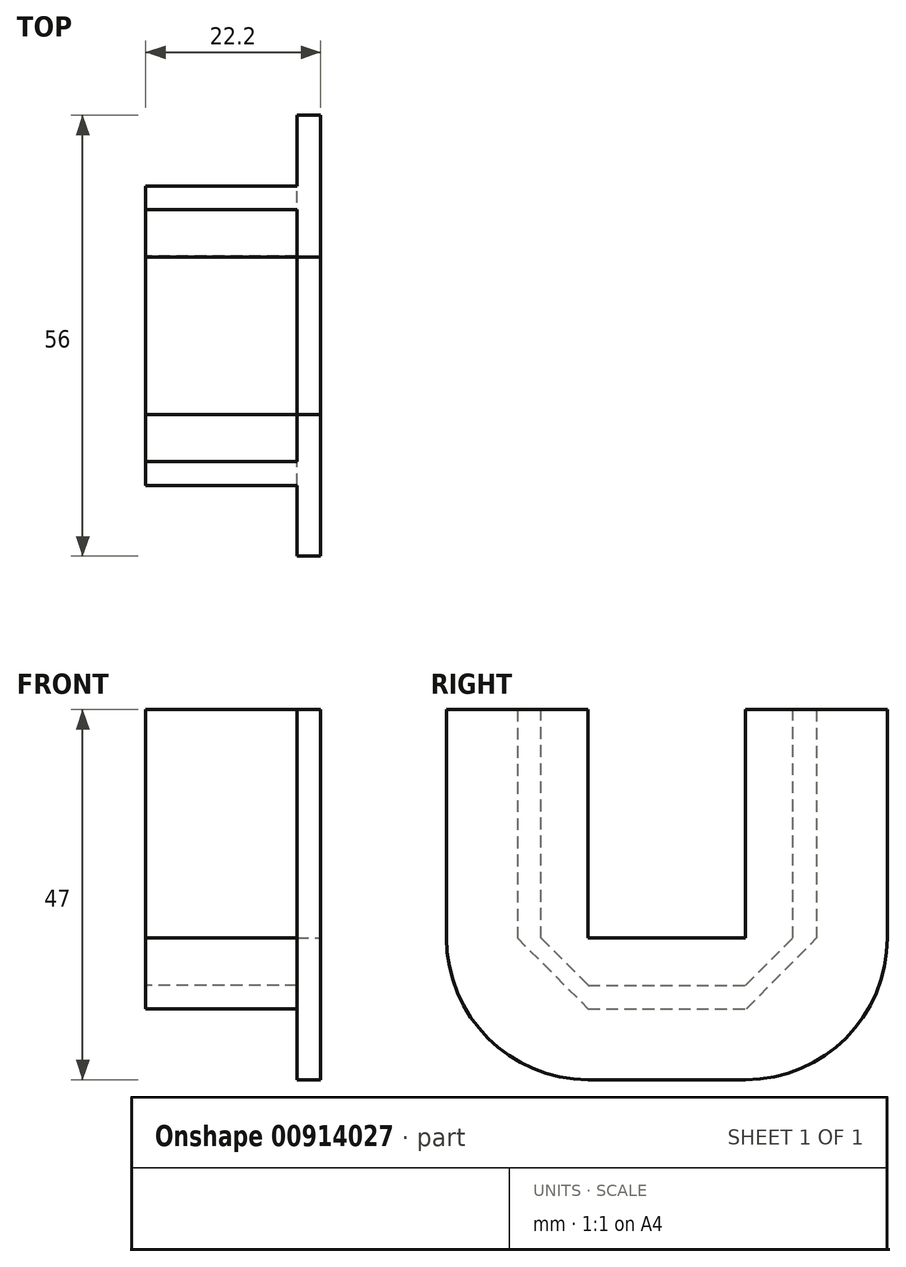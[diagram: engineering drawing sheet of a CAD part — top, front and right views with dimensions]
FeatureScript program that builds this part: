
annotation { "Feature Type Name" : "Feature", "Feature Type Description" : "" }
export const myFeature = defineFeature(function(context is Context, id is Id, definition is map)
    precondition{}
    {
        {
            var Q0;
            Q0=qCreatedBy(makeId("Right.planeOp"),FACE);
            var sketch = newSketch(context, id + "F0", { "sketchPlane" : qUnion([Q0])});
            skLineSegment(sketch, "E0", {"start": v(0, -35) * mm, "end": v(10, -35) * mm});
            skLineSegment(sketch, "E1", {"start": v(16, -29) * mm, "end": v(16, 0) * mm});
            skLineSegment(sketch, "E2", {"start": v(16, 0) * mm, "end": v(19, 0) * mm});
            skLineSegment(sketch, "E3", {"start": v(19, 0) * mm, "end": v(19, -29) * mm});
            skLineSegment(sketch, "E4", {"start": v(10, -38) * mm, "end": v(6, -38) * mm});
            skLineSegment(sketch, "E5", {"start": v(0, -35) * mm, "end": v(0, 0) * mm, "construction": true});
            skLineSegment(sketch, "E6.MirrorCS", {"start": v(-16, 0) * mm, "end": v(-19, 0) * mm});
            skLineSegment(sketch, "E7.MirrorCS", {"start": v(-16, -29) * mm, "end": v(-16, 0) * mm});
            skLineSegment(sketch, "E8.MirrorCS", {"start": v(-19, 0) * mm, "end": v(-19, -29) * mm});
            skLineSegment(sketch, "E9.MirrorCS", {"start": v(0, -35) * mm, "end": v(-10, -35) * mm});
            skLineSegment(sketch, "E10.MirrorCS", {"start": v(-10, -38) * mm, "end": v(-6, -38) * mm});
            skLineSegment(sketch, "E11", {"start": v(-6, -38) * mm, "end": v(6, -38) * mm});
            skLineSegment(sketch, "E12", {"start": v(19, 0) * mm, "end": v(28, 0) * mm});
            skLineSegment(sketch, "E13", {"start": v(28, 0) * mm, "end": v(28, -29) * mm});
            skLineSegment(sketch, "E14", {"start": v(10, -47) * mm, "end": v(-10, -47) * mm});
            skLineSegment(sketch, "E15", {"start": v(-28, -29) * mm, "end": v(-28, 0) * mm});
            skLineSegment(sketch, "E16", {"start": v(-28, 0) * mm, "end": v(-19, 0) * mm});
            skPoint(sketch, "E17", {"position": v(-10, -29) * mm});
            skPoint(sketch, "E18", {"position": v(10, -29) * mm});
            skArc(sketch, "E19", {"start": v(-28, -29) * mm, "mid": v(-22.73, -41.73) * mm, "end": v(-10, -47) * mm});
            skArc(sketch, "E20", {"start": v(10, -47) * mm, "mid": v(22.73, -41.73) * mm, "end": v(28, -29) * mm});
            skLineSegment(sketch, "E21", {"start": v(-16, -29) * mm, "end": v(-10, -35) * mm});
            skLineSegment(sketch, "E22", {"start": v(-19, -29) * mm, "end": v(-10, -38) * mm});
            skLineSegment(sketch, "E23", {"start": v(10, -35) * mm, "end": v(16, -29) * mm});
            skLineSegment(sketch, "E24", {"start": v(10.1, -38.03) * mm, "end": v(19, -29) * mm});
            skLineSegment(sketch, "E25", {"start": v(-10, -29) * mm, "end": v(10, -29) * mm});
            skLineSegment(sketch, "E26", {"start": v(10, -29) * mm, "end": v(10, 0) * mm});
            skLineSegment(sketch, "E27", {"start": v(10, 0) * mm, "end": v(16, 0) * mm});
            skLineSegment(sketch, "E28", {"start": v(-10, -29) * mm, "end": v(-10, 0) * mm});
            skLineSegment(sketch, "E29", {"start": v(-10, 0) * mm, "end": v(-16, 0) * mm});
            skLineSegment(sketch, "E30", {"start": v(-19, 0) * mm, "end": v(-16, 0) * mm});
            skSolve(sketch);
        }
        {
            var Q0;
            Q0=qCreatedBy(makeId("Right.planeOp"),FACE);
            var sketch = newSketch(context, id + "F1", { "sketchPlane" : qUnion([Q0])});
            skLineSegment(sketch, "E31.0", {"start": v(-19, 0) * mm, "end": v(-19, -29) * mm});
            skLineSegment(sketch, "E31.1", {"start": v(-19, -29) * mm, "end": v(-10, -38) * mm});
            skLineSegment(sketch, "E31.2", {"start": v(-10, -38) * mm, "end": v(-6, -38) * mm});
            skLineSegment(sketch, "E31.3", {"start": v(-6, -38) * mm, "end": v(6, -38) * mm});
            skLineSegment(sketch, "E31.4", {"start": v(10.12, -38) * mm, "end": v(6, -38) * mm});
            skLineSegment(sketch, "E31.5", {"start": v(10.12, -38) * mm, "end": v(19, -29) * mm});
            skLineSegment(sketch, "E31.6", {"start": v(19, 0) * mm, "end": v(19, -29) * mm});
            skLineSegment(sketch, "E31.7", {"start": v(16, -29) * mm, "end": v(16, 0) * mm});
            skLineSegment(sketch, "E31.8", {"start": v(10, -35) * mm, "end": v(16, -29) * mm});
            skLineSegment(sketch, "E31.9", {"start": v(0, -35) * mm, "end": v(10, -35) * mm});
            skLineSegment(sketch, "E31.10", {"start": v(0, -35) * mm, "end": v(-10, -35) * mm});
            skLineSegment(sketch, "E31.11", {"start": v(-16, -29) * mm, "end": v(-10, -35) * mm});
            skLineSegment(sketch, "E31.12", {"start": v(-16, -29) * mm, "end": v(-16, 0) * mm});
            skLineSegment(sketch, "E31.13", {"start": v(-16, 0) * mm, "end": v(-19, 0) * mm});
            skLineSegment(sketch, "E31.14", {"start": v(16, 0) * mm, "end": v(19, 0) * mm});
            skPoint(sketch, "E32.orphan", {"position": v(10, -38) * mm});
            skPoint(sketch, "E33.orphan", {"position": v(10.1, -38.03) * mm});
            skSolve(sketch);
        }
        {
            var Q0;
            Q0 = qSketchRegion(id + "F1", true);
            extrude(context, id + "F2", {"entities" : qUnion([Q0]), "endBound" : BoundingType.SYMMETRIC, "depth" : 22.2 * mm, "offsetDistance" : 25 * mm});
        }
        {
            var Q0;
            Q0=makeQuery(id+"F2.opExtrude","CAP_FACE",FACE,{"disambiguationData":[OSD([sQuery(id+"F1.wireOp",EDGE,"E31.0"),sQuery(id+"F1.wireOp",EDGE,"E31.1"),sQuery(id+"F1.wireOp",EDGE,"E31.2"),sQuery(id+"F1.wireOp",EDGE,"E31.3"),sQuery(id+"F1.wireOp",EDGE,"E31.4"),sQuery(id+"F1.wireOp",EDGE,"E31.5"),sQuery(id+"F1.wireOp",EDGE,"E31.6"),sQuery(id+"F1.wireOp",EDGE,"E31.7"),sQuery(id+"F1.wireOp",EDGE,"E31.8"),sQuery(id+"F1.wireOp",EDGE,"E31.9"),sQuery(id+"F1.wireOp",EDGE,"E31.10"),sQuery(id+"F1.wireOp",EDGE,"E31.11"),sQuery(id+"F1.wireOp",EDGE,"E31.12"),sQuery(id+"F1.wireOp",EDGE,"E31.13"),sQuery(id+"F1.wireOp",EDGE,"E31.14")])],"isStart":false});
            var sketch = newSketch(context, id + "F3", { "sketchPlane" : qUnion([Q0])});
            skLineSegment(sketch, "E34.0", {"start": v(-28, -29) * mm, "end": v(-28, 0) * mm});
            skArc(sketch, "E34.1", {"start": v(-28, -29) * mm, "mid": v(-22.73, -41.73) * mm, "end": v(-10, -47) * mm});
            skLineSegment(sketch, "E34.2", {"start": v(10, -47) * mm, "end": v(-10, -47) * mm});
            skArc(sketch, "E34.3", {"start": v(10, -47) * mm, "mid": v(22.73, -41.73) * mm, "end": v(28, -29) * mm});
            skLineSegment(sketch, "E34.4", {"start": v(28, 0) * mm, "end": v(28, -29) * mm});
            skLineSegment(sketch, "E35", {"start": v(-28, 0) * mm, "end": v(-19, 0) * mm});
            skLineSegment(sketch, "E36", {"start": v(28, 0) * mm, "end": v(19, 0) * mm});
            skSolve(sketch);
        }
        {
            var Q0;
            Q0 = qSketchRegion(id + "F3", true);
            var Q1;
            Q1=makeQuery(id+"F3.imprint","IMPRINT",FACE,{"disambiguationData":[TD([[makeQuery(id+"F3.imprint","IMPRINT",EDGE,{"derivedFrom":sQuery(id+"F3.wireOp",EDGE,"E34.0")}),-1.0]])]});
            extrude(context, id + "F4", {"entities" : qUnion([Q0, Q1]), "operationType" : NewBodyOperationType.ADD, "oppositeDirection" : true, "depth" : 3 * mm, "offsetDistance" : 25 * mm});
        }
        {
            var Q0;
            {var subQ0=sQuery(id+"F1.wireOp",EDGE,"E31.6");var subQ1=sQuery(id+"F1.wireOp",EDGE,"E31.5");var subQ2=sQuery(id+"F1.wireOp",EDGE,"E31.4");var subQ3=sQuery(id+"F1.wireOp",EDGE,"E31.3");var subQ4=sQuery(id+"F1.wireOp",EDGE,"E31.2");var subQ5=sQuery(id+"F1.wireOp",EDGE,"E31.1");var subQ6=sQuery(id+"F1.wireOp",EDGE,"E31.0");Q0=makeQuery(id+"F4.boolean.opBoolean","MERGE",FACE,{"derivedFrom":[makeQuery(id+"F2.opExtrude","CAP_FACE",FACE,{"disambiguationData":[OSD([subQ6,subQ5,subQ4,subQ3,subQ2,subQ1,subQ0,sQuery(id+"F1.wireOp",EDGE,"E31.7"),sQuery(id+"F1.wireOp",EDGE,"E31.8"),sQuery(id+"F1.wireOp",EDGE,"E31.9"),sQuery(id+"F1.wireOp",EDGE,"E31.10"),sQuery(id+"F1.wireOp",EDGE,"E31.11"),sQuery(id+"F1.wireOp",EDGE,"E31.12"),sQuery(id+"F1.wireOp",EDGE,"E31.13"),sQuery(id+"F1.wireOp",EDGE,"E31.14")])],"isStart":false}),makeQuery(id+"F4.opExtrude","CAP_FACE",FACE,{"disambiguationData":[OSD([subQ6,subQ5,subQ4,subQ3,subQ2,subQ1,subQ0,sQuery(id+"F3.wireOp",EDGE,"E34.0"),sQuery(id+"F3.wireOp",EDGE,"E34.1"),sQuery(id+"F3.wireOp",EDGE,"E34.2"),sQuery(id+"F3.wireOp",EDGE,"E34.3"),sQuery(id+"F3.wireOp",EDGE,"E34.4"),sQuery(id+"F3.wireOp",EDGE,"E35"),sQuery(id+"F3.wireOp",EDGE,"E36")])],"isStart":true})]});}
            var sketch = newSketch(context, id + "F5", { "sketchPlane" : qUnion([Q0])});
            skLineSegment(sketch, "E37.0", {"start": v(10, -29) * mm, "end": v(10, 0) * mm});
            skLineSegment(sketch, "E38.0", {"start": v(10, 0) * mm, "end": v(16, 0) * mm});
            skLineSegment(sketch, "E38.1", {"start": v(-10, -29) * mm, "end": v(10, -29) * mm});
            skLineSegment(sketch, "E38.2", {"start": v(-10, -29) * mm, "end": v(-10, 0) * mm});
            skLineSegment(sketch, "E38.3", {"start": v(-10, 0) * mm, "end": v(-16, 0) * mm});
            skLineSegment(sketch, "E39.0", {"start": v(-16, -29) * mm, "end": v(-16, 0) * mm});
            skLineSegment(sketch, "E39.1", {"start": v(-16, -29) * mm, "end": v(-10, -35) * mm});
            skLineSegment(sketch, "E39.2", {"start": v(0, -35) * mm, "end": v(-10, -35) * mm});
            skLineSegment(sketch, "E39.3", {"start": v(0, -35) * mm, "end": v(10, -35) * mm});
            skLineSegment(sketch, "E39.4", {"start": v(10, -35) * mm, "end": v(16, -29) * mm});
            skLineSegment(sketch, "E39.5", {"start": v(16, -29) * mm, "end": v(16, 0) * mm});
            skSolve(sketch);
        }
        {
            var Q0;
            Q0 = qSketchRegion(id + "F5", true);
            extrude(context, id + "F6", {"entities" : qUnion([Q0]), "operationType" : NewBodyOperationType.ADD, "oppositeDirection" : true, "depth" : 3 * mm, "offsetDistance" : 25 * mm});
        }
    });
